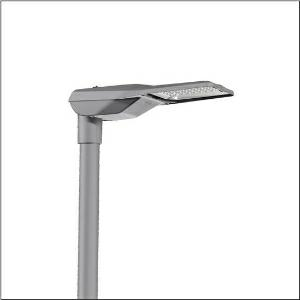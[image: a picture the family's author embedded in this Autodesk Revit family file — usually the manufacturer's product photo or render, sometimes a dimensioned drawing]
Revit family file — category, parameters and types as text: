
# Revit family: streetlight_sl_21_mini___st0_5a_5xe2b33s08jb_541c
name_source: partatom
category: Lighting Fixtures
units: mm (PartAtom-declared; Revit-internal decimal feet)

## family parameters
Cut with Voids When Loaded = No
Host = Face
Light Source = No
Part Type = Normal
Room Calculation Point = No
Round Connector Dimension = Use Diameter
Shared = No

## types (1)
- --- (1 x LED, 12940 lm, 88.6 W, 3000K)
    Apparent Load = 89 VA
    CIE Flux Codes = 43 76 97 100 100
    Color Rendering = 70
    Color Temperature = 3000K
    Default Elevation = 1800 mm
    Description = Streetlight SL 21 mini, mast luminaire, primary light control with lens, of PMMA, primary optical cover: cover, of toughened safety glass, transparent, light distribution: ST0.5a, light emission: direct distribution, primary light characteristic: asymmetric, installation type: side-entry, post-top, LED, High Power LED, rated luminous flux: 12.940lm, luminous efficacy: 146lm/W, light colour: 730, colour temperature: 3000K, control gear: D4i, control: overheat protection, constant luminous flux control, time-dependent luminous flux control, flexible luminous flux parameterisation, pre-setting: logarithmic dimming characteristic, mains connection: 220..240V, AC, 50/60Hz, start of lifetime: 89W, end of service life: 92W, reduction: 41W, luminaire housing, of diecast aluminium, powder-coated, Siteco® metallic grey (DB 702S), corrosivity category C5 mid according to DIN EN ISO 12944, please order mast flange separately, inclination adjustable: 0°, 5°, 10°, 15°, sealing non-destructively replaceable, multi-level sealing system, length: 628mm, width: 235mm, height: 110mm, mast flange for spigot size: 42mm (side-entry): 5XC10008XM4, 60/48mm (side-entry/post-top): 5XC10108XM2, 76/60mm (side-entry/post-top): 5XC10108XM1, mounting height: 4..8m, Smart Interface above, protection rating (complete): IP66, insulation class (complete): insulation class II (safety insulation), certification: CE, ENEC, ENEC+, VDE, impact resistance: IK10, permissible operating ambient temperature for outdoor applications: -40..+50°C, standard-compliant lighting for roads and squares, packaging unit: 1 piece

Light Distribution: ST0.5a
    Height = 110 mm
    Lamp = 1 x LED
    Lamp Light Flux = 12940 lm
    Lamp Power = 88.6 W
    Lamp count = 1
    Length = 625 mm
    Luminous efficacy = 146 lm/W
    Manufacturer = Siteco
    ModVariant = No
    Model = 5XE2B33S08JB
    Number of Poles = 1
    OnlyDefault = Yes
    Power Factor = 1
    Product Name = Streetlight SL 21 mini | ST0.5a
    Product group = mast luminaire | pylon top
    ProductGroupID = 6100
    Protection Class = Protection class II
    Protection Degree = IP 66
    RLX_Detail_Level = 1
    RLX_Emergency_Light_Flux = 0 lm
    RLX_Emergency_Type = 0
    RLX_Emergency_Type_DB = No
    RlxData = <blob elided: 37365 chars, md5=0bb52b18>
    Socket = socket
    Standby Power = 0 W
    System Light Flux = 12940 lm
    System Power = 89 W
    Type Comments = factory setting: luminous flux: 100 % | dim-lin: 254 | 915 mA
    Type Image = l_1003515.jpg
    URL = http://relux.com
    VarID = @adj_012365
    Voltage = 0 V
    Weight = 0.00 kg
    Width = 234 mm

## geometry (parser evidence)
native form markers: Blend x4, Sweep x11
no freeform markers — native parametric forms only
